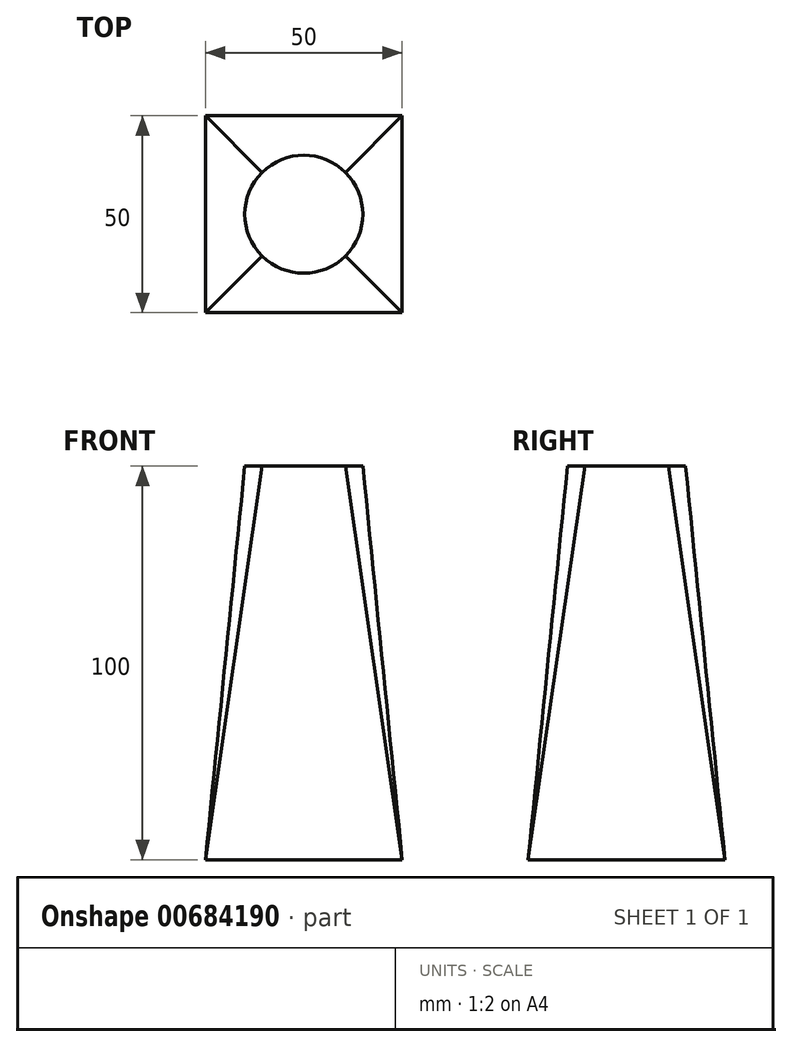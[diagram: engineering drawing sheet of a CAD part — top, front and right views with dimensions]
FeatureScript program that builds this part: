
annotation { "Feature Type Name" : "Feature", "Feature Type Description" : "" }
export const myFeature = defineFeature(function(context is Context, id is Id, definition is map)
    precondition{}
    {
        {
            var Q0;
            Q0=qCreatedBy(makeId("Top.planeOp"),FACE);
            cPlane(context, id + "F0", {"entities" : qUnion([Q0]), "cplaneType" : CPlaneType.OFFSET, "offset" : 100 * mm, "width" : 152.4 * mm, "height" : 152.4 * mm});
        }
        {
            var Q0;
            Q0=qCreatedBy(makeId("Top.planeOp"),FACE);
            var sketch = newSketch(context, id + "F1", { "sketchPlane" : qUnion([Q0])});
            skLineSegment(sketch, "E0.bottom", {"start": v(-25, 25) * mm, "end": v(25, 25) * mm});
            skLineSegment(sketch, "E0.top", {"start": v(-25, -25) * mm, "end": v(25, -25) * mm});
            skLineSegment(sketch, "E0.left", {"start": v(-25, 25) * mm, "end": v(-25, -25) * mm});
            skLineSegment(sketch, "E0.right", {"start": v(25, 25) * mm, "end": v(25, -25) * mm});
            skPoint(sketch, "E0.middle", {"position": v(0, 0) * mm});
            skSolve(sketch);
        }
        {
            var Q0;
            Q0=qCreatedBy(id+"F0.planeOp",FACE);
            var sketch = newSketch(context, id + "F2", { "sketchPlane" : qUnion([Q0])});
            skCircle(sketch, "E1", {"center": v(0, 0) * mm, "radius": 15 * mm});
            skSolve(sketch);
        }
        {
            var Q0;
            Q0=makeQuery(id+"F1.imprint","IMPRINT",FACE,{"disambiguationData":[TD([[makeQuery(id+"F1.imprint","IMPRINT",EDGE,{"derivedFrom":sQuery(id+"F1.wireOp",EDGE,"E0.bottom")}),-1.0]])]});
            var Q1;
            Q1=makeQuery(id+"F2.imprint","IMPRINT",FACE,{"disambiguationData":[TD([[makeQuery(id+"F2.imprint","IMPRINT",EDGE,{"derivedFrom":sQuery(id+"F2.wireOp",EDGE,"E1")}),1.0]])]});
            loft(context, id + "F3", {"sheetProfilesArray" : [{ "sheetProfileEntities" : qUnion([Q0]) }, { "sheetProfileEntities" : qUnion([Q1]) }]});
        }
    });
